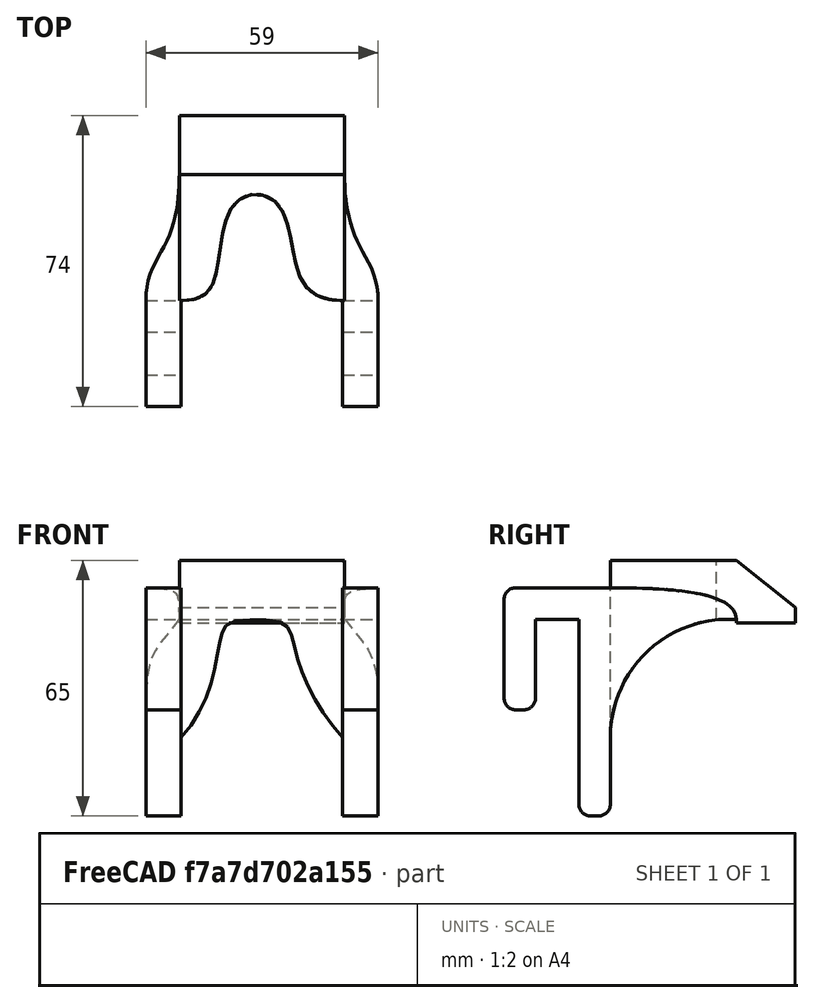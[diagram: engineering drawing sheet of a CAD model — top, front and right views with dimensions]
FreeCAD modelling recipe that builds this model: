
FCSTD DOCUMENT  (FreeCAD 0.20R29177 +426 (Git))
Label: PS5ControllerChargerHolder
License: All rights reserved
LicenseURL: http://en.wikipedia.org/wiki/All_rights_reserved
objects: Part::MultiFuse×2, Sketcher::SketchObject×2, PartDesign::Body×2, Part::Wedge×1, Part::Box×1, PartDesign::Pad×1, Part::Extrusion×1, Part::MultiCommon×1, PartDesign::FeatureBase×1, Part::Fillet×1, Mesh::Feature×1
note: 14 computed .brp shape members not serialized (recipe doc carries the construction recipe); baked Part::Feature solids carry a one-line shape summary decoded from their .brp

FEATURE [Part::Wedge] Wedge
  AttacherType = Attacher::AttachEngine3D
  X2max = 42
  X2min = 0
  Xmax = 42
  Xmin = 0
  Ymax = 15
  Ymin = 0
  Z2max = 3
  Z2min = -1
  Zmax = 15
  Zmin = -1
FEATURE [Part::Box] Box  label="Cube"
  AttacherType = Attacher::AttachEngine3D
  Height = 15
  Length = 42
  Placement = pos=(0,-32,0) rot=(0,0,1;0rad)
  Width = 32
FEATURE [Part::MultiFuse] Fusion
  Placement = pos=(8.5,0,0) rot=(0,0,1;0rad)
  Shapes = -> [Wedge,Box]
FEATURE [Sketcher::SketchObject] Sketch
  FullyConstrained = true
  Placement = pos=(0,0,0) rot=(0.57735,0.57735,0.57735;2.0944rad)
  sketch-geometry (26):
    g0: LineSegment StartX=-32 StartY=8 StartZ=0 EndX=-56 EndY=8 EndZ=0
    g1: LineSegment StartX=-59 StartY=5 StartZ=0 EndX=-59 EndY=-20 EndZ=0
    g2: LineSegment StartX=-56 StartY=-23 StartZ=0 EndX=-54 EndY=-23 EndZ=0
    g3: LineSegment StartX=-51 StartY=-20 StartZ=0 EndX=-51 EndY=0 EndZ=0
    g4: LineSegment StartX=-51 StartY=0 StartZ=0 EndX=-40 EndY=0 EndZ=0
    g5: LineSegment StartX=-40 StartY=0 StartZ=0 EndX=-40 EndY=-47 EndZ=0
    g6: LineSegment StartX=-37 StartY=-50 StartZ=0 EndX=-35 EndY=-50 EndZ=0
    g7: LineSegment StartX=-32 StartY=-47 StartZ=0 EndX=-32 EndY=-30 EndZ=0
    g8: LineSegment StartX=-2 StartY=-1.208e-13 StartZ=0 EndX=0 EndY=-1.208e-13 EndZ=0
    g9: ArcOfCircle CenterX=-2 CenterY=-30 CenterZ=0 NormalX=0 NormalY=0 NormalZ=1 AngleXU=0 Radius=30 StartAngle=1.5708 EndAngle=3.14159
    g10: ArcOfCircle CenterX=-56 CenterY=5 CenterZ=0 NormalX=0 NormalY=0 NormalZ=1 AngleXU=0 Radius=3 StartAngle=1.5708 EndAngle=3.14159
    g11: GeomPoint X=-59 Y=8 Z=0
    g12: ArcOfCircle CenterX=-56 CenterY=-20 CenterZ=0 NormalX=0 NormalY=0 NormalZ=1 AngleXU=0 Radius=3 StartAngle=3.14159 EndAngle=4.71239
    g13: GeomPoint X=-59 Y=-23 Z=0
    g14: ArcOfCircle CenterX=-54 CenterY=-20 CenterZ=0 NormalX=0 NormalY=0 NormalZ=1 AngleXU=0 Radius=3 StartAngle=4.71239 EndAngle=6.28319
    g15: GeomPoint X=-51 Y=-23 Z=0
    g16: ArcOfCircle CenterX=-37 CenterY=-47 CenterZ=0 NormalX=0 NormalY=0 NormalZ=1 AngleXU=0 Radius=3 StartAngle=3.14159 EndAngle=4.71239
    g17: GeomPoint X=-40 Y=-50 Z=0
    g18: ArcOfCircle CenterX=-35 CenterY=-47 CenterZ=0 NormalX=0 NormalY=0 NormalZ=1 AngleXU=0 Radius=3 StartAngle=4.71239 EndAngle=6.28319
    g19: GeomPoint X=-32 Y=-50 Z=0
    g20-g23: Circle x4 (B-spline internal-alignment scaffolding for g24; pole/knot coordinates omitted)
    g24: BSplineCurve PolesCount=4 KnotsCount=2 Degree=3 IsPeriodic=0
    g25: GeomPoint X=0 Y=-1.208e-13 Z=0
  constraints (61):
    c: Horizontal(g0)
    c: Vertical(g1)
    c: Horizontal(g2)
    c: Vertical(g3)
    c: Coincident(g3,g4)
    c: Horizontal(g4)
    c: Coincident(g4,g5)
    c: Vertical(g5)
    c: Horizontal(g6)
    c: Vertical(g7)
    c: Tangent(g7,g9) = 1.5708
    c: Tangent(g8,g9) = 1.5708
    c: PointOnObject(g11,g0)
    c: PointOnObject(g11,g1)
    c: Tangent(g0,g10) = -1.5708
    c: Tangent(g1,g10) = -1.5708
    c: PointOnObject(g13,g1)
    c: PointOnObject(g13,g2)
    c: Tangent(g1,g12) = -1.5708
    c: Tangent(g2,g12) = -1.5708
    c: PointOnObject(g15,g2)
    c: PointOnObject(g15,g3)
    c: Tangent(g2,g14) = -1.5708
    c: Tangent(g3,g14) = -1.5708
    c: PointOnObject(g17,g5)
    c: PointOnObject(g17,g6)
    c: Tangent(g5,g16) = -1.5708
    c: Tangent(g6,g16) = -1.5708
    c: PointOnObject(g19,g6)
    c: PointOnObject(g19,g7)
    c: Tangent(g6,g18) = -1.5708
    c: Tangent(g7,g18) = -1.5708
    c: DistanceY(g4,g0) = 8
    c: Radius(g10) = 3
    c: DistanceX(g1,g3) = 8
    c: DistanceX(g4,g4) = 11
    c: DistanceY(g15,g3) = 23
    c: DistanceX(g5,g7) = 8
    c: Equal(g12,g10)
    c: Equal(g12,g14)
    c: Equal(g14,g16)
    c: Equal(g16,g18)
    c: DistanceY(g17,g4) = 50
    c: Radius(g9) = 30
    c: Horizontal(g8)
    c: Vertical(g7,g0)
    c: DistanceX(g0,g8) = 32
    c: Weight(g20) = 1
    c: Equal(g20,g21)
    c: PointOnObject(g21,g-2)
    c: Equal(g20,g22)
    c: Equal(g20,g23)
    c: Coincident(g24,g0)
    c: InternalAlignment(g20-g23 -> g24) x4
    c: Horizontal(g0,g22)
    c: DistanceY(g8,g21) = 6
    c: DistanceX(g0,g22) = 20
    c: PointOnObject(g4,g-1)
    c: Coincident(g8,g24)
    c: Coincident(g8,g25)
    c: Coincident(g-1,g8)
FEATURE [PartDesign::Pad] Pad
  Direction = (1,0,0)
  Length = 59
  Length2 = 10
  Placement = pos=(0,0,0) rot=(0.57735,0.57735,0.57735;2.0944rad)
  Profile = -> Sketch
  ReferenceAxis = -> Sketch [N_Axis]
  Type = 0
FEATURE [PartDesign::Body] Body
  Group = -> [Sketch,Pad]
  Origin = -> Origin
  Tip = -> Pad
FEATURE [Part::MultiFuse] Fusion001
  Shapes = -> [Fusion,Body]
FEATURE [Sketcher::SketchObject] Sketch001
  ExternalGeometry = -> [Fusion001]
  FullyConstrained = true
  sketch-geometry (40):
    g0: LineSegment StartX=0 StartY=-32 StartZ=0 EndX=0 EndY=-67 EndZ=0
    g1: LineSegment StartX=59 StartY=-67 StartZ=0 EndX=59 EndY=-32 EndZ=0
    g2: LineSegment StartX=8.5 StartY=0 StartZ=0 EndX=8.5 EndY=45 EndZ=0
    g3: LineSegment StartX=8.5 StartY=45 StartZ=0 EndX=50.5 EndY=45 EndZ=0
    g4: LineSegment StartX=50.5 StartY=45 StartZ=0 EndX=50.5 EndY=0 EndZ=0
    g5: LineSegment StartX=0 StartY=-67 StartZ=0 EndX=9 EndY=-67 EndZ=0
    g6: LineSegment StartX=9 StartY=-67 StartZ=0 EndX=9 EndY=-32 EndZ=0
    g7: LineSegment StartX=50 StartY=-32 StartZ=0 EndX=50 EndY=-67 EndZ=0
    g8: LineSegment StartX=50 StartY=-67 StartZ=0 EndX=59 EndY=-67 EndZ=0
    g9: LineSegment StartX=0 StartY=-32 StartZ=0 EndX=8.5 EndY=0 EndZ=0
    g10: LineSegment StartX=50.5 StartY=0 StartZ=0 EndX=59 EndY=-32 EndZ=0
    g11-g18: Circle x8 (B-spline internal-alignment scaffolding for g19; pole/knot coordinates omitted)
    g19: BSplineCurve PolesCount=8 KnotsCount=6 Degree=3 IsPeriodic=0
    g20-g25: GeomPoint x6 (B-spline internal-alignment scaffolding for g19; pole/knot coordinates omitted)
    g26-g29: Circle x4 (B-spline internal-alignment scaffolding for g30; pole/knot coordinates omitted)
    g30: BSplineCurve PolesCount=4 KnotsCount=2 Degree=3 IsPeriodic=0
    g31: GeomPoint X=0 Y=-32 Z=0
    g32: GeomPoint X=8.5 Y=0 Z=0
    g33-g36: Circle x4 (B-spline internal-alignment scaffolding for g37; pole/knot coordinates omitted)
    g37: BSplineCurve PolesCount=4 KnotsCount=2 Degree=3 IsPeriodic=0
    g38: GeomPoint X=59 Y=-32 Z=0
    g39: GeomPoint X=50.5 Y=0 Z=0
  constraints (78):
    c: PointOnObject(g0,g-2)
    c: Vertical(g1)
    c: DistanceY(g0,g0) = 35
    c: Vertical(g2)
    c: Horizontal(g3)
    c: Vertical(g4)
    c: DistanceY(g2,g2) = 45
    c: Coincident(g0,g5)
    c: Horizontal(g5)
    c: Coincident(g5,g6)
    c: Vertical(g6)
    c: Vertical(g7)
    c: Coincident(g7,g8)
    c: Coincident(g8,g1)
    c: Horizontal(g8)
    c: DistanceX(g8,g8) = 9
    c: DistanceX(g5,g5) = 9
    c: Equal(g7,g6)
    c: Coincident(g9,g0)
    c: Coincident(g10,g1)
    c: Equal(g9,g10)
    c: Equal(g2,g4)
    c: Horizontal(g5,g7)
    c: PointOnObject(g4,g-1)
    c: Coincident(g4,g10)
    c: Coincident(g2,g9)
    c: Coincident(g2,g3)
    c: DistanceX(g3,g3) = 42
    c: Coincident(g4,g3)
    c: PointOnObject(g7,g-5)
    c: DistanceX(g0,g1) = 59
    c: PointOnObject(g0,g-5)
    c: PointOnObject(g1,g-5)
    c: Vertical(g0)
    c: Weight(g11) = 1
    c: Coincident(g19,g6)
    c: Equal(g11, g12-g18) x7
    c: Coincident(g19,g7)
    c: InternalAlignment(g11-g18 -> g19) x8
    c: InternalAlignment(g20-g25 -> g19) x6
    c: Horizontal(g14,g15)
    c: DistanceY(g7,g15) = 28
    c: DistanceX(g16,g17) = 8
    c: Vertical(g13,g14)
    c: Vertical(g15,g16)
    c: Weight(g26) = 1
    c: Coincident(g30,g0)
    c: Equal(g26,g27)
    c: PointOnObject(g27,g-2)
    c: Equal(g26,g28)
    c: Equal(g26,g29)
    c: Coincident(g30,g2)
    c: InternalAlignment(g26-g29 -> g30) x4
    c: InternalAlignment(g31,g30)
    c: InternalAlignment(g32,g30)
    c: Weight(g33) = 1
    c: Coincident(g37,g1)
    c: Equal(g33,g34)
    c: Equal(g33,g35)
    c: Equal(g33,g36)
    c: Coincident(g37,g4)
    c: InternalAlignment(g33-g36 -> g37) x4
    c: InternalAlignment(g38,g37)
    c: InternalAlignment(g39,g37)
    c: Horizontal(g27,g28)
    c: Horizontal(g35,g34)
    c: Horizontal(g28,g35)
    c: DistanceY(g1,g34) = 12
    c: Vertical(g35,g4)
    c: Vertical(g28,g2)
    c: Vertical(g34,g1)
    c: PointOnObject(g12,g-5)
    c: PointOnObject(g17,g-5)
    c: DistanceX(g6,g12) = 5
    c: DistanceX(g17,g7) = 5
    c: Horizontal(g13,g16)
    c: DistanceX(g12,g13) = 5
    c: DistanceY(g17,g16) = 3
FEATURE [Part::Extrusion] Extrude
  Base = -> Sketch001
  Dir = (0,0,1)
  DirMode = 2
  FaceMakerClass = Part::FaceMakerBullseye
  LengthFwd = 100
  LengthRev = 0
  Solid = true
  Symmetric = true
FEATURE [Part::MultiCommon] Common
  Shapes = -> [Fusion001,Extrude]
FEATURE [PartDesign::FeatureBase] BaseFeature
  BaseFeature = -> Common
FEATURE [PartDesign::Body] Body001
  BaseFeature = -> Common
  Group = -> [BaseFeature]
  Origin = -> Origin001
  Tip = -> BaseFeature
FEATURE [Part::Fillet] Fillet
  Base = -> BaseFeature
  Edges = 9 edges r=1: [Edge52,Edge76,Edge77,Edge79,Edge80,Edge82,Edge98,Edge99,Edge116]
FEATURE [Mesh::Feature] Mesh  label="Fillet (Meshed)"
